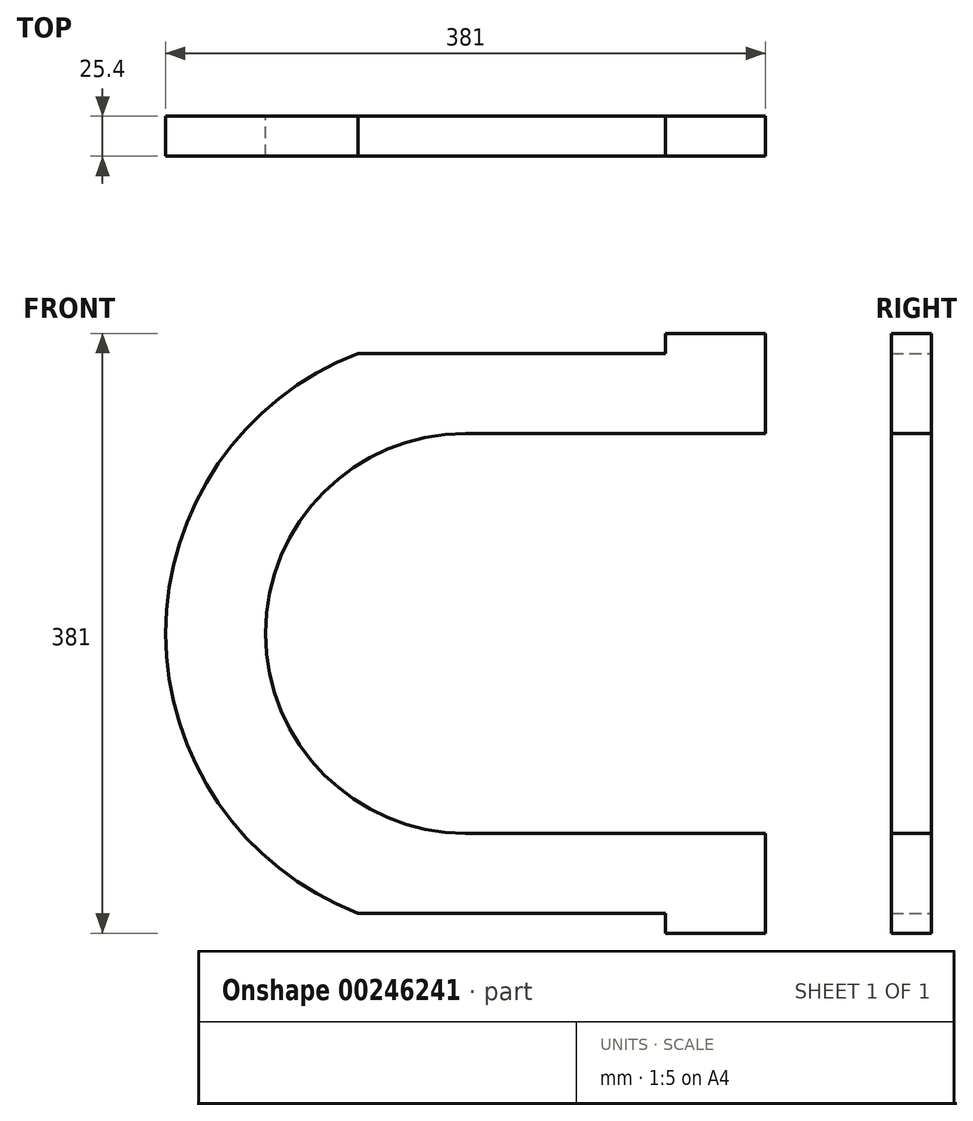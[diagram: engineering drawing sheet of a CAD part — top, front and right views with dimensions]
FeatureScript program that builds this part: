
annotation { "Feature Type Name" : "Feature", "Feature Type Description" : "" }
export const myFeature = defineFeature(function(context is Context, id is Id, definition is map)
    precondition{}
    {
        {
            var Q0;
            Q0=qCreatedBy(makeId("Front.planeOp"),FACE);
            var sketch = newSketch(context, id + "F0", { "sketchPlane" : qUnion([Q0])});
            skLineSegment(sketch, "E0.bottom", {"start": v(127, -177.8) * mm, "end": v(-68.4, -177.8) * mm});
            skLineSegment(sketch, "E0.top", {"start": v(127, 177.8) * mm, "end": v(-68.4, 177.8) * mm});
            skLineSegment(sketch, "E0.left", {"start": v(190.5, -177.8) * mm, "end": v(190.5, -127) * mm});
            skPoint(sketch, "E0.middle", {"position": v(0, 0) * mm});
            skArc(sketch, "E1", {"start": v(0, 127) * mm, "mid": v(-127, 0) * mm, "end": v(0, -127) * mm});
            skLineSegment(sketch, "E2", {"start": v(0, -127) * mm, "end": v(190.5, -127) * mm});
            skLineSegment(sketch, "E3", {"start": v(0, 127) * mm, "end": v(190.5, 127) * mm});
            skLineSegment(sketch, "E4.bottom", {"start": v(190.5, -127) * mm, "end": v(127, -127) * mm});
            skLineSegment(sketch, "E4.top", {"start": v(190.5, -190.5) * mm, "end": v(127, -190.5) * mm});
            skLineSegment(sketch, "E4.left", {"start": v(190.5, -127) * mm, "end": v(190.5, -190.5) * mm});
            skLineSegment(sketch, "E4.right", {"start": v(127, -177.8) * mm, "end": v(127, -190.5) * mm});
            skLineSegment(sketch, "E5.bottom", {"start": v(190.5, 127) * mm, "end": v(127, 127) * mm});
            skLineSegment(sketch, "E5.top", {"start": v(190.5, 190.5) * mm, "end": v(127, 190.5) * mm});
            skLineSegment(sketch, "E5.left", {"start": v(190.5, 127) * mm, "end": v(190.5, 190.5) * mm});
            skLineSegment(sketch, "E5.right", {"start": v(127, 177.8) * mm, "end": v(127, 190.5) * mm});
            skLineSegment(sketch, "E6.trimOffspring", {"start": v(190.5, 127) * mm, "end": v(190.5, 177.8) * mm});
            skPoint(sketch, "E7.orphan", {"position": v(-190.5, -177.8) * mm});
            skPoint(sketch, "E8.orphan", {"position": v(-190.5, 177.8) * mm});
            skArc(sketch, "E9.trimOffspring", {"start": v(-68.4, 177.8) * mm, "mid": v(-190.5, 0) * mm, "end": v(-68.4, -177.8) * mm});
            skSolve(sketch);
        }
        {
            var Q0;
            Q0=makeQuery(id+"F0.imprint","IMPRINT",FACE,{"disambiguationData":[TD([[makeQuery(id+"F0.imprint","IMPRINT",EDGE,{"derivedFrom":sQuery(id+"F0.wireOp",EDGE,"E0.bottom")}),-1.0]])]});
            extrude(context, id + "F1", {"entities" : qUnion([Q0]), "depth" : 25.4 * mm});
        }
    });
